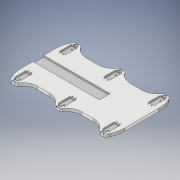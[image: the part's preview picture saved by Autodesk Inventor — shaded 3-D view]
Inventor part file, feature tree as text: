
AUTODESK INVENTOR PART (.ipt)
format: ipt  version: 2017 (Build 210142000, 142)  size: 374,272 bytes
history: native  units: mm
features: extrude x6, sketch x6, fillet x3
ambient origin geometry x8: Origin, YZ Plane, XZ Plane, XY Plane, X Axis, Y Axis, Z Axis, Center Point
bodies: Solid1 (feature_tree)
feature tree (15):
  extrude  "Extrusion1"  Depth=82.5mm
  extrude  "Extrusion2"  Depth=10.0mm
  extrude  "Extrusion3"  Depth=10.0mm
  fillet  "Fillet1"  [1 undecoded]
  fillet  "Fillet2"  Radius=11.5mm
  fillet  "Fillet3"  Radius=5.0mm
  extrude  "Extrusion10"  Depth=40.5mm
  extrude  "Extrusion11"  Depth=5.0mm
  extrude  "Extrusion12"  TaperAngle=0.0deg  [1 undecoded]
  sketch  "Sketch1"  dims[d0=30.0mm d1=82.5mm]
  sketch  "Sketch2"  dims[d2=26.75mm d3=10.0mm]
  sketch  "Sketch3"  dims[d4=120.0mm d5=10.0mm d6=0.0mm d7=11.5mm d8=5.0mm]
  sketch  "Sketch10"  dims[d9=20.0mm d10=40.5mm]
  sketch  "Sketch11"  dims[d11=5.0mm d12=5.0mm]
  sketch  "Sketch12"  dims[d13=5.0mm d14=0.0mm d17=4.0mm d18=4.0mm d19=4.5mm d25=2.75mm d26=2.75mm d27=2.75mm d28=5.0mm d29=0.0mm d37=10.0mm d38=50.0mm d69=100.0mm d70=3.0mm d75=10.0mm d76=4.0mm d77=10.0mm d78=0.0mm d81=7.5mm d82=2.0mm d83=0.0mm d84=36.0mm d85=50.0mm d86=5.0mm d87=0.0mm]
note: 2 required parameter values undecoded (feature->parameter linkage not recoverable at this tier; creation-order binding heuristic only, values carry confidence <= 0.55)
